# Revit family: Haworth_UniGroupToo_Panel_Solid
name_source: partatom
category: Furniture Systems
revit_build: Autodesk Revit 2018 (Build: 20170223_1515(x64)
units: mm (PartAtom-declared; Revit-internal decimal feet)

## family parameters
Always vertical = Yes
Cut with Voids When Loaded = No
OmniClass Number = 23.40.70.14.64.21
OmniClass Title = Systems Furniture
Part Type = Normal
Room Calculation Point = No
Round Connector Dimension = Use Diameter
Shared = No
Work Plane-Based = No

## types (42) — shared parameters
Assembly Code = E2020500
Bottom Trim Width = 3/8"
Custom Size = No
Description = Haworth - UniGroup Too - Panel - Solid
Glide Height = 3/8"
Manufacturer = Haworth
Max. Height = 80"
Max. Width = 60"
Min. Height = 32"
Min. Width = 24"
Model = Haworth - UniGroup Too - Panel - Solid
Offset Front = 4 3/8"
Panel Depth = 1/2"
Raceway Finish = Haworth _ Paint _ Graphite
Raceway Panel Height = 4"
Revision Number = 2
Size = Verify Final Dim. w/ Haworth
Standard Heights = 32, 40, 48, 56, 64, 72, 80 inches
Standard Widths = 24, 30, 36, 42, 48, 60 inches
Sustainability Info = http://www.haworth.com
Top Trim Height = 1/2"
Trim Depth = 2"
Trim Finish = Haworth _ Metal _ Brushed Aluminum
URL = www.haworth.com
URL - Product = http://www.haworth.com
Warranty = http://www.haworth.com

## per-type parameters (varying)
| type | Actual Height | Actual Width | Height | Panel Height | Raceway Panel Width | Rail Height | Width |
| 24w 32h | 32" | 24" | 32" | 27 1/8" | 24" | 31 1/2" | 24" |
| 30w 32h | 32" | 30" | 32" | 27 1/8" | 30" | 31 1/2" | 30" |
| 36w 32h | 32" | 36" | 32" | 27 1/8" | 36" | 31 1/2" | 36" |
| 42w 32h | 32" | 42" | 32" | 27 1/8" | 42" | 31 1/2" | 42" |
| 48w 32h | 32" | 48" | 32" | 27 1/8" | 48" | 31 1/2" | 48" |
| 60w 32h | 32" | 60" | 32" | 27 1/8" | 60" | 31 1/2" | 60" |
| 24w 40h | 40" | 24" | 40" | 35 1/8" | 24" | 39 1/2" | 24" |
| 30w 40h | 40" | 30" | 40" | 35 1/8" | 30" | 39 1/2" | 30" |
| 36w 40h | 40" | 36" | 40" | 35 1/8" | 36" | 39 1/2" | 36" |
| 42w 40h | 40" | 42" | 40" | 35 1/8" | 42" | 39 1/2" | 42" |
| 48w 40h | 40" | 48" | 40" | 35 1/8" | 48" | 39 1/2" | 48" |
| 60w 40h | 40" | 60" | 40" | 35 1/8" | 60" | 39 1/2" | 60" |
| 24w 48h | 48" | 24" | 48" | 43 1/8" | 24" | 47 1/2" | 24" |
| 30w 48h | 48" | 30" | 48" | 43 1/8" | 30" | 47 1/2" | 30" |
| 36w 48h | 48" | 36" | 48" | 43 1/8" | 36" | 47 1/2" | 36" |
| 42w 48h | 48" | 42" | 48" | 43 1/8" | 42" | 47 1/2" | 42" |
| 48w 48h | 48" | 48" | 48" | 43 1/8" | 48" | 47 1/2" | 48" |
| 60w 48h | 48" | 60" | 48" | 43 1/8" | 60" | 47 1/2" | 60" |
| 24w 56h | 56" | 24" | 56" | 51 1/8" | 24" | 55 1/2" | 24" |
| 30w 56h | 56" | 30" | 56" | 51 1/8" | 30" | 55 1/2" | 30" |
| 36w 56h | 56" | 36" | 56" | 51 1/8" | 36" | 55 1/2" | 36" |
| 42w 56h | 56" | 42" | 56" | 51 1/8" | 42" | 55 1/2" | 42" |
| 48w 56h | 56" | 48" | 56" | 51 1/8" | 48" | 55 1/2" | 48" |
| 60w 56h | 56" | 60" | 56" | 51 1/8" | 60" | 55 1/2" | 60" |
| 24w 64h | 64" | 24" | 64" | 59 1/8" | 24" | 63 1/2" | 24" |
| 30w 64h | 64" | 30" | 64" | 59 1/8" | 30" | 63 1/2" | 30" |
| 36w 64h | 64" | 36" | 64" | 59 1/8" | 36" | 63 1/2" | 36" |
| 42w 64h | 64" | 42" | 64" | 59 1/8" | 42" | 63 1/2" | 42" |
| 48w 64h | 64" | 48" | 64" | 59 1/8" | 48" | 63 1/2" | 48" |
| 60w 64h | 64" | 60" | 64" | 59 1/8" | 60" | 63 1/2" | 60" |
| 24w 72h | 72" | 24" | 72" | 67 1/8" | 24" | 71 1/2" | 24" |
| 30w 72h | 72" | 30" | 72" | 67 1/8" | 30" | 71 1/2" | 30" |
| 36w 72h | 72" | 36" | 72" | 67 1/8" | 36" | 71 1/2" | 36" |
| 42w 72h | 72" | 42" | 72" | 67 1/8" | 42" | 71 1/2" | 42" |
| 48w 72h | 72" | 48" | 72" | 67 1/8" | 48" | 71 1/2" | 48" |
| 60w 72h | 72" | 60" | 72" | 67 1/8" | 60" | 71 1/2" | 60" |
| 24w 80h | 80" | 24" | 80" | 75 1/8" | 24" | 79 1/2" | 24" |
| 30w 80h | 80" | 30" | 80" | 75 1/8" | 30" | 79 1/2" | 30" |
| 36w 80h | 80" | 36" | 80" | 75 1/8" | 36" | 79 1/2" | 36" |
| 42w 80h | 80" | 42" | 80" | 75 1/8" | 42" | 79 1/2" | 42" |
| 48w 80h | 80" | 48" | 80" | 75 1/8" | 48" | 79 1/2" | 48" |
| 60w 80h | 80" | 60" | 80" | 75 1/8" | 60" | 79 1/2" | 60" |

## geometry (parser evidence)
native form markers: Sweep x8
no freeform markers — native parametric forms only
